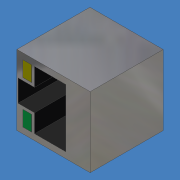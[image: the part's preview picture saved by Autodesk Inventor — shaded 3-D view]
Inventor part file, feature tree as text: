
AUTODESK INVENTOR PART (.ipt)
format: ipt  version: 2011 (Build 150239000, 239)  size: 133,632 bytes
history: native  units: mm (DEFAULTED — no unit token found)
features: extrude x3, sketch x3, mirror x1
ambient origin geometry x8: Origin, YZ Plane, XZ Plane, XY Plane, X Axis, Y Axis, Z Axis, Center Point
bodies: Solid1 (feature_tree)
feature tree (7):
  extrude  "Extrusion1"  Depth=16.2052mm
  extrude  "Extrusion2"  Depth=13.462mm
  extrude  "Extrusion3"  Depth=3.81mm
  mirror  "Mirror1"
  sketch  "Sketch1"  dims[d0=16.9164mm d1=16.2052mm]
  sketch  "Sketch2"  dims[d2=16.8656mm d3=0.0mm d4=13.462mm]
  sketch  "Sketch3"  dims[d5=0.254mm d6=3.81mm d7=5.08mm d8=5.588mm d9=10.16mm d10=0.0mm d11=0.635mm d12=0.635mm d13=2.032mm d14=0.0254mm d15=0.0mm]
